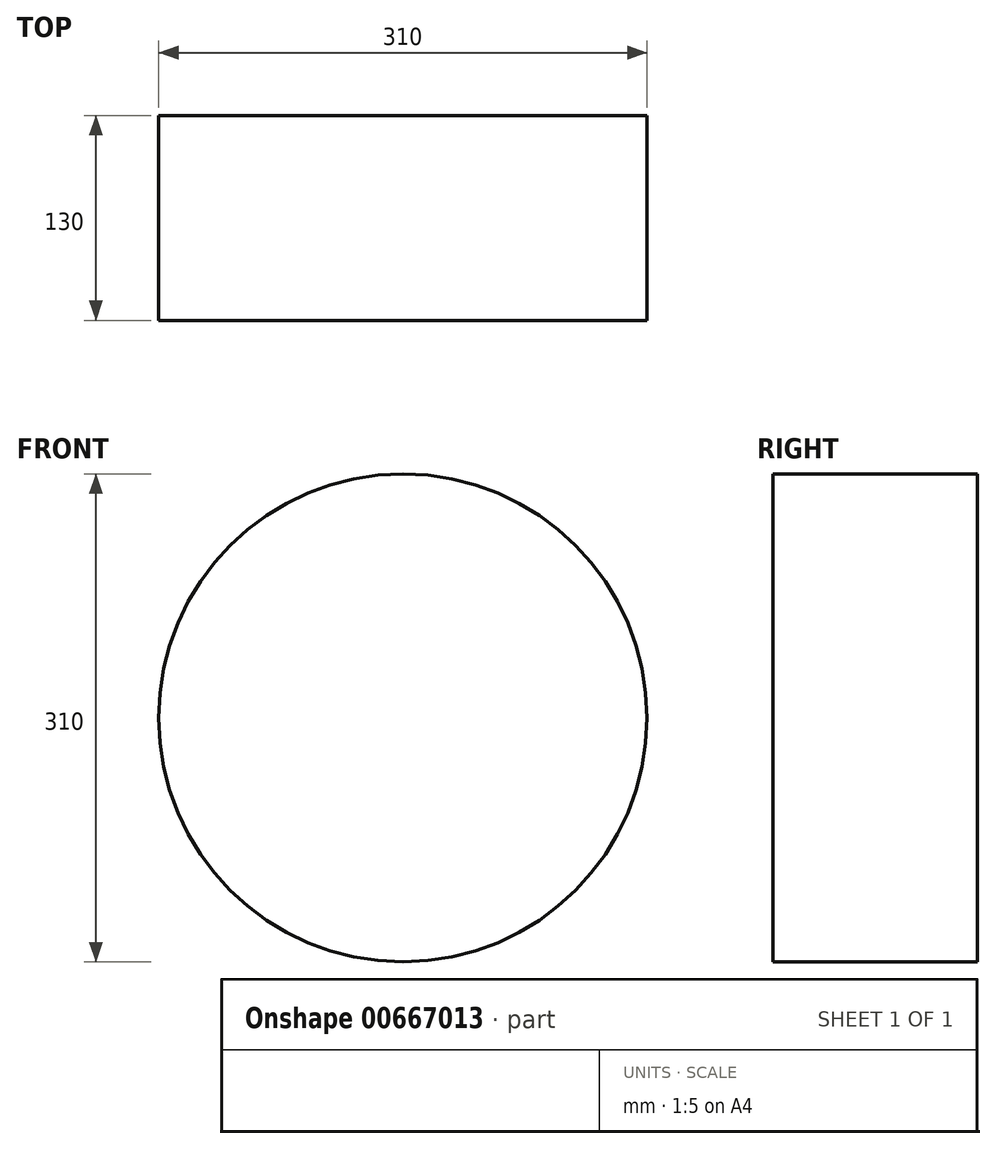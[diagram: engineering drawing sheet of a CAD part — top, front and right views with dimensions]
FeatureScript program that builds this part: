
annotation { "Feature Type Name" : "Feature", "Feature Type Description" : "" }
export const myFeature = defineFeature(function(context is Context, id is Id, definition is map)
    precondition{}
    {
        {
            var Q0;
            Q0=qCreatedBy(makeId("Front.planeOp"),FACE);
            var sketch = newSketch(context, id + "F0", { "sketchPlane" : qUnion([Q0])});
            skCircle(sketch, "E0", {"center": v(0, 0) * mm, "radius": 155 * mm});
            skSolve(sketch);
        }
        {
            var Q0;
            Q0 = qSketchRegion(id + "F0", true);
            extrude(context, id + "F1", {"entities" : qUnion([Q0]), "depth" : 130 * mm, "offsetDistance" : 25 * mm});
        }
    });
